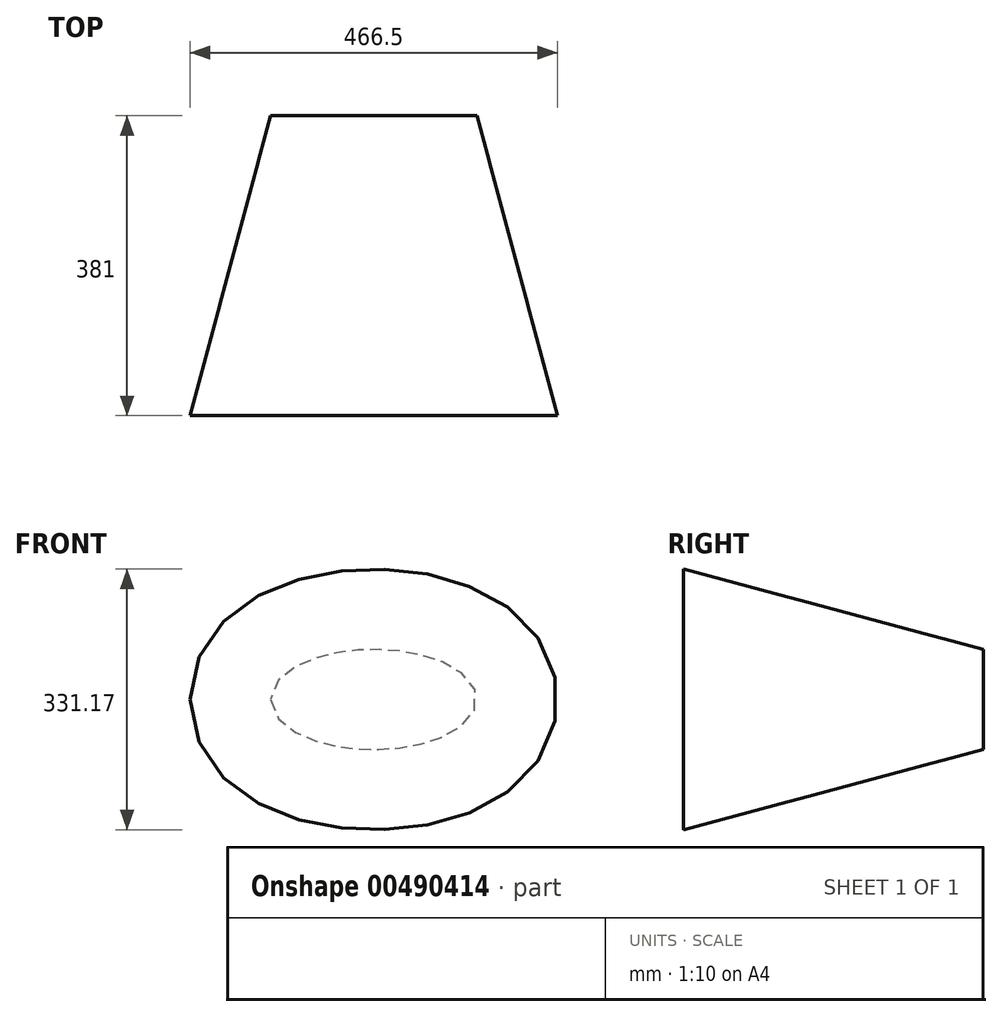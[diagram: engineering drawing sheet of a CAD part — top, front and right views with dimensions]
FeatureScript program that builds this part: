
annotation { "Feature Type Name" : "Feature", "Feature Type Description" : "" }
export const myFeature = defineFeature(function(context is Context, id is Id, definition is map)
    precondition{}
    {
        {
            var Q0;
            Q0=qCreatedBy(makeId("Front.planeOp"),FACE);
            var sketch = newSketch(context, id + "F0", { "sketchPlane" : qUnion([Q0])});
            skEllipse(sketch, "E0", {"center": v(0, 13.5) * mm, "majorRadius": 131.16 * mm, "minorRadius": 63.5 * mm, "majorAxis": v(1, 0)});
            skSolve(sketch);
        }
        {
            var Q0;
            Q0 = qSketchRegion(id + "F0", true);
            extrude(context, id + "F1", {"entities" : qUnion([Q0]), "depth" : 381 * mm, "offsetDistance" : 25.4 * mm, "hasDraft" : true, "draftAngle" : 15 * degree});
        }
    });
